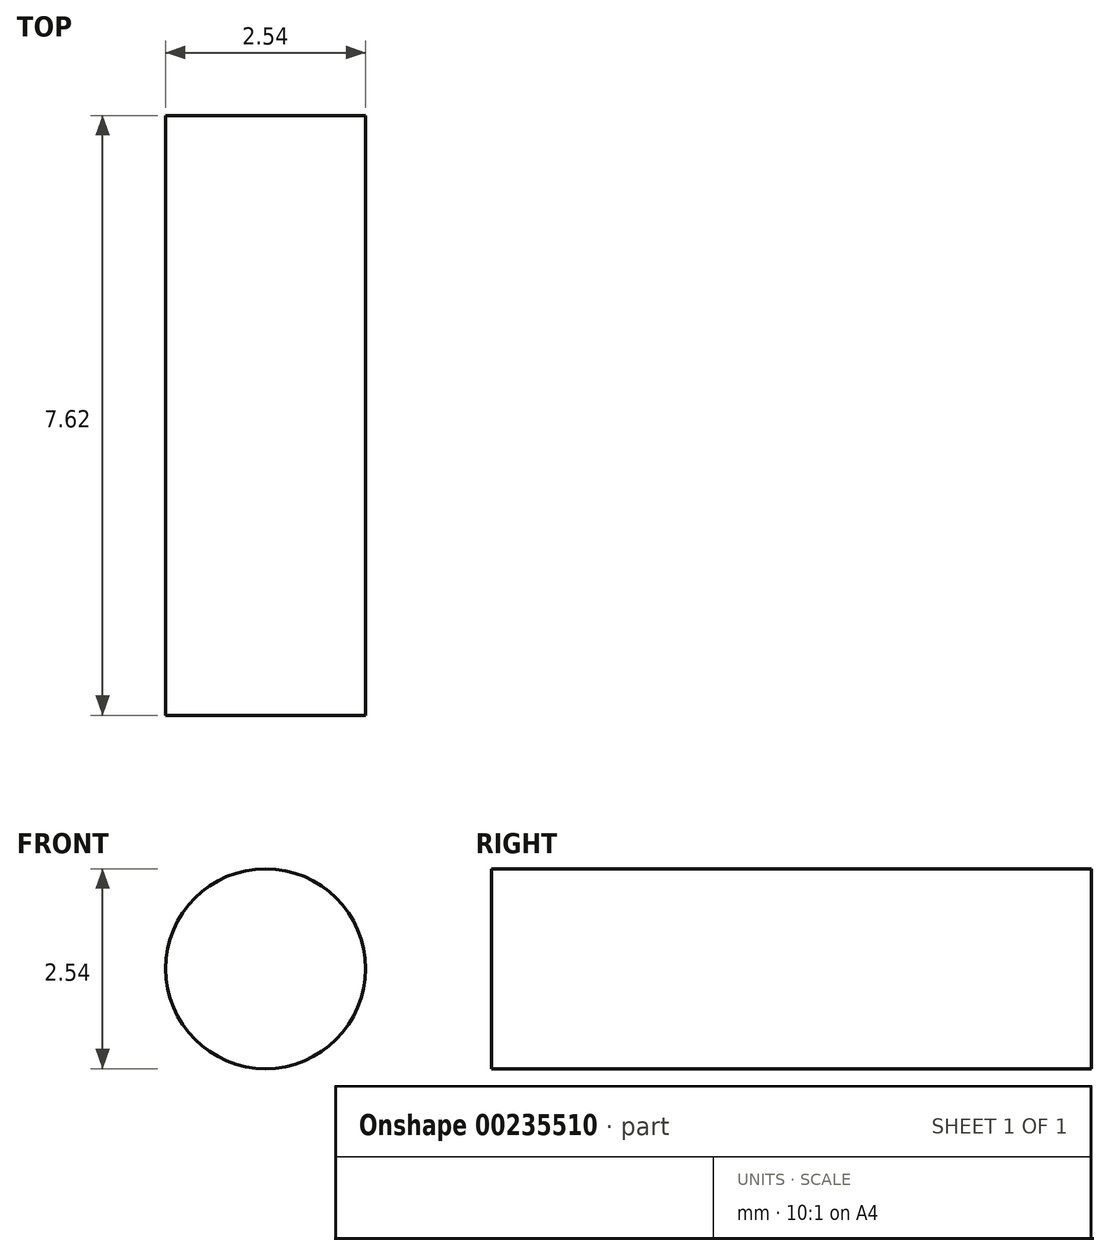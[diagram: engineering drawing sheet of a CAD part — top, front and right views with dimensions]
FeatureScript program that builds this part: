
annotation { "Feature Type Name" : "Feature", "Feature Type Description" : "" }
export const myFeature = defineFeature(function(context is Context, id is Id, definition is map)
    precondition{}
    {
        {
            var Q0;
            Q0=qCreatedBy(makeId("Front.planeOp"),FACE);
            var sketch = newSketch(context, id + "F0", { "sketchPlane" : qUnion([Q0])});
            skCircle(sketch, "E0", {"center": v(0, 0) * mm, "radius": 1.27 * mm});
            skSolve(sketch);
        }
        {
            var Q0;
            Q0 = qSketchRegion(id + "F0", true);
            extrude(context, id + "F1", {"entities" : qUnion([Q0]), "depth" : 7.62 * mm});
        }
    });
